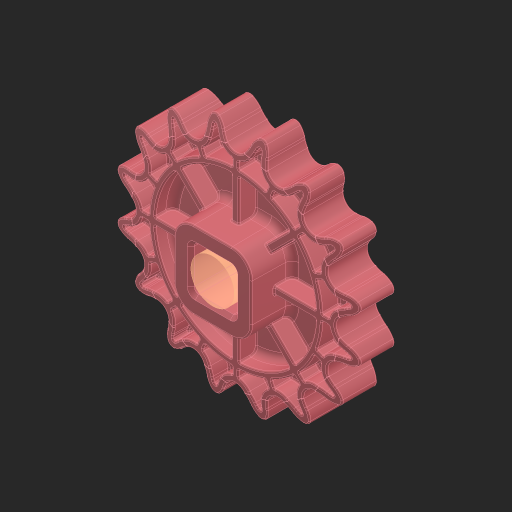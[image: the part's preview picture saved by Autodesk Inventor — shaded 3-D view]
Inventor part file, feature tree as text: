
AUTODESK INVENTOR PART (.ipt)
format: ipt  version: 2023 (Build 270158000, 158)  size: 4,780,544 bytes
history: native  units: in
note: dims shown in document units (in); Inventor stores cm internally (conversion verified against a paired STEP export)
features: sketch x1, other x1, chamfer x1, extrude x1
ambient origin geometry x8: Origin, YZ Plane, XZ Plane, XY Plane, X Axis, Y Axis, Z Axis, Center Point
bodies: Solid1 (feature_tree)
feature tree (4):
  sketch  "Sketch1"  dims[d0=0.25in d1=0.3937in d2=0.0in d3=0.0197in d4=1.9685in]
  other  "Srf1"
  chamfer  "Chamfer3"  Distance=0.3937in
  extrude  "ExtrusionSrf1"  Depth=0.3937in
